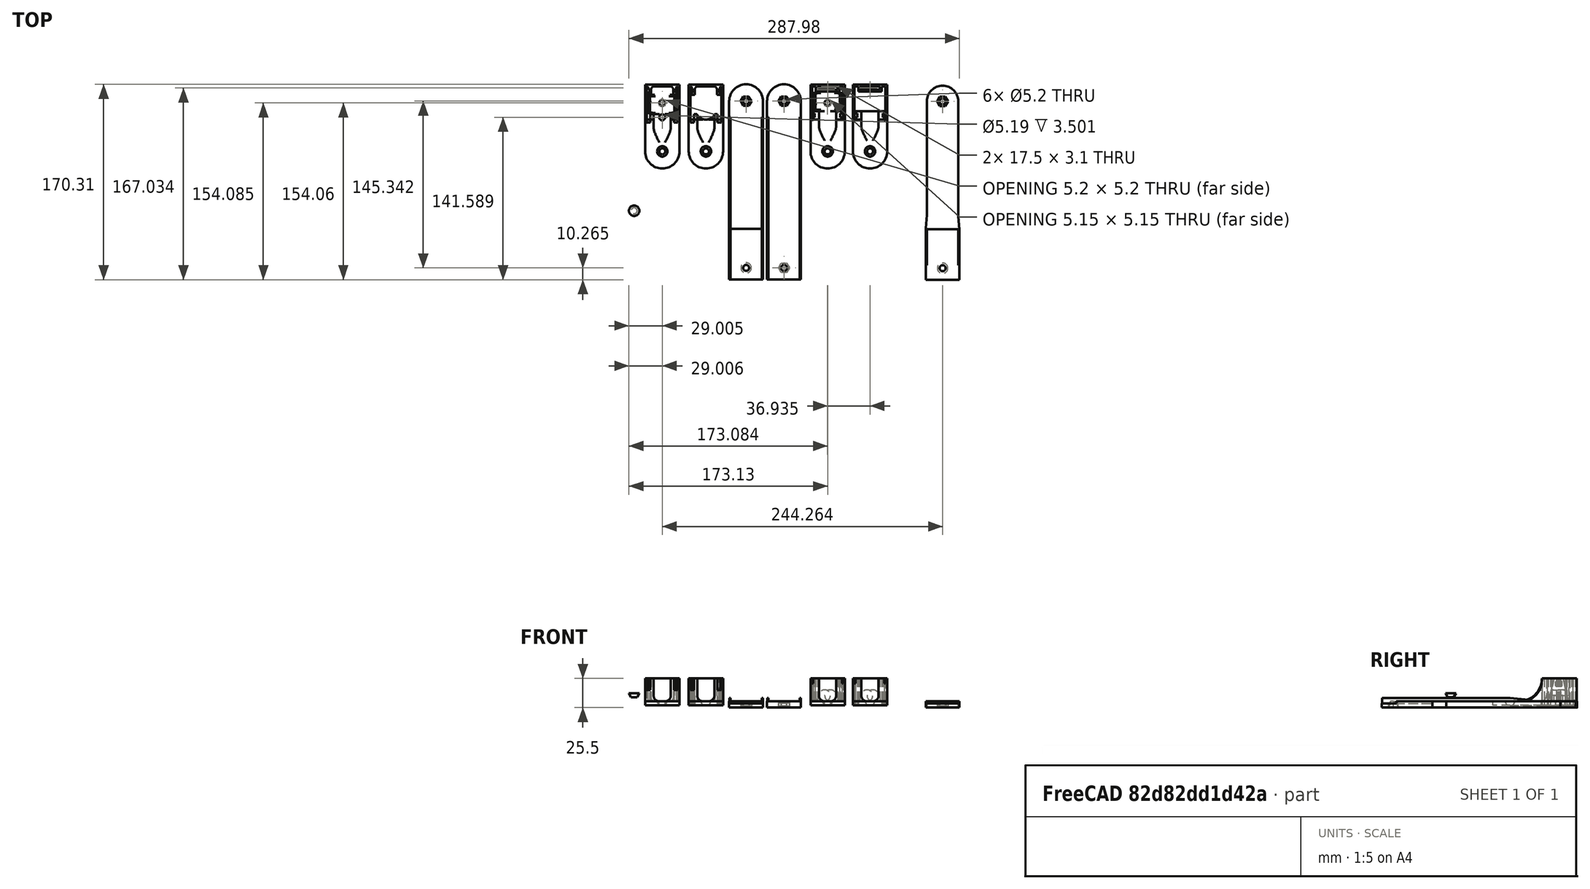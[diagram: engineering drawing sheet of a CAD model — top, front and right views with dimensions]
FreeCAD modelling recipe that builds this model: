
FCSTD DOCUMENT  (FreeCAD 0.20R29177 +426 (Git))
Label: lamp.hanger
License: All rights reserved
LicenseURL: http://en.wikipedia.org/wiki/All_rights_reserved
objects: Part::Cut×5, Part::Feature×5, Part::Extrusion×5, Part::MultiFuse×4, Part::Part2DObjectPython×4, Part::FeaturePython×2, App::DocumentObjectGroup×1, Part::Cone×1
note: 26 computed .brp shape members not serialized (recipe doc carries the construction recipe); baked Part::Feature solids carry a one-line shape summary decoded from their .brp

FEATURE [Part::MultiFuse] Fusion005002002014004003003002009002010004002003006003008008004007002004006006004008003005011012024  label="Reversed_Closed"
  Placement = pos=(139,-7e-15,-2.8e-14) rot=(0,0,1;0rad)
FEATURE [Part::Cut] Cut004006005004002008019023005008  label="Reversed_Open"
FEATURE [Part::MultiFuse] Fusion005002002014004003003002009002010004002003006003008008004007002004006006004008003005011013  label="Straight_Open"
FEATURE [Part::Feature] Fusion005002002014004003003002009002010004002003006003008008004007002004006006004008003005011006001  label="Console_Nut"
  shape: bbox 29.42 x 170 x 8.5 mm, 29 faces (baked)
FEATURE [Part::Feature] Fusion005002002014004003003002009002010004002003006003008008004007002004003001  label="Console_Screw"
  shape: bbox 29.42 x 170 x 8.5 mm, 24 faces (baked)
FEATURE [Part::Feature] Cut004006005004002008019023005046_solid  label="Straight_Closed"
  shape: bbox 29.86 x 73.08 x 23.5 mm, 156 faces (baked)
FEATURE [Part::Part2DObjectPython] Rectangle  # Draft 2D object (typed FeaturePython)
  ChamferSize = 0
  Columns = 1
  FilletRadius = 0
  Height = 7.4
  Length = 25
  MakeFace = true
  Placement = pos=(-687.019,-1.87622,16.3661) rot=(0,0,1;0rad)
  Rows = 1
FEATURE [Part::Extrusion] Extrusion
  Base = -> Rectangle
  Dir = (0,2.193e-13,-109.626)
  DirMode = 0
  FaceMakerClass = Part::FaceMakerBullseye
  LengthFwd = 0
  LengthRev = 0
  Solid = true
  Symmetric = false
FEATURE [Part::Cut] Cut
  Base = -> Fusion005002002014004003003002009002010004002003006003008008004007002004006006004008003005011013
  Tool = -> Extrusion
FEATURE [Part::Feature] Face
  Placement = pos=(54.9167,-4e-15,-2.5e-14) rot=(0,0,1;0rad)
  shape: bbox 29.86 x 8.799 x 4.951e-06 mm, 1 faces, 0 solids (baked)
FEATURE [Part::Extrusion] Extrusion001
  Base = -> Face
  Dir = (8.24e-14,-1.179e-13,15.3738)
  DirMode = 0
  FaceMakerClass = Part::FaceMakerBullseye
  LengthFwd = 0
  LengthRev = 0
  Placement = pos=(38.0168,1.181e-13,-15.3738) rot=(0,0,1;0rad)
  Solid = true
  Symmetric = false
FEATURE [Part::Feature] Face001
  Placement = pos=(92.9335,1.141e-13,-15.3738) rot=(0,0,1;0rad)
  shape: bbox 29.86 x 8.799 x 4.951e-06 mm, 1 faces, 0 solids (baked)
FEATURE [Part::Extrusion] Extrusion002
  Base = -> Face001
  Dir = (-4.36e-14,6.23e-14,-8.12616)
  DirMode = 0
  FaceMakerClass = Part::FaceMakerBullseye
  LengthFwd = 0
  LengthRev = 0
  Solid = true
  Symmetric = false
FEATURE [Part::MultiFuse] Fusion
  Shapes = -> [Extrusion002,Extrusion001]
FEATURE [Part::MultiFuse] Fusion005002002014004003003002009002010004002003006003008008004007002004006006004008003005011012025  label="Straight_Open001"
  Shapes = -> [Cut,Fusion]
FEATURE [Part::Part2DObjectPython] Rectangle001  # Draft 2D object (typed FeaturePython)
  ChamferSize = 0
  Columns = 1
  FilletRadius = 0
  Height = 42.3954
  Length = 36.2167
  MakeFace = true
  Placement = pos=(-548.432,-30.8896,16.3661) rot=(0,0,1;0rad)
  Rows = 1
  Support = -> [Cut004006005004002008019023005008]
FEATURE [Part::FeaturePython] Slice  # WARN: FeaturePython — macro-defined, semantics opaque (R4)
  Base = -> Cut004006005004002008019023005008
  Mode = 1
  Tolerance = 0
  Tools = -> [Rectangle001]
FEATURE [Part::FeaturePython] Slice_child0  label="Slice.0"  # WARN: FeaturePython — macro-defined, semantics opaque (R4)
  Base = -> Slice
  FilterType = 1
  Invert = false
  OverrideMaxVal = 0
  WindowFrom = 80
  WindowTo = 100
  items = 0
FEATURE [App::DocumentObjectGroup] GrExplode_Slice  label="Exploded Slice"
  Group = -> [Slice_child0]
FEATURE [Part::Cone] Cone
  Angle = 360
  AttacherType = Attacher::AttachEngine3D
  Height = 3.5
  Placement = pos=(-737,-103,0) rot=(0,0,1;0rad)
  Radius1 = 2.6
  Radius2 = 4.55
FEATURE [Part::Part2DObjectPython] Circle  # Draft 2D object (typed FeaturePython)
  FirstAngle = 0
  LastAngle = 0
  MakeFace = true
  Placement = pos=(-674.529,-14.4762,-3.63395) rot=(0,0,1;0rad)
  Radius = 9
FEATURE [Part::Extrusion] Extrusion003
  Base = -> Circle
  Dir = (0,0,190.437)
  DirMode = 0
  FaceMakerClass = Part::FaceMakerBullseye
  LengthFwd = 0
  LengthRev = 0
  Placement = pos=(0,0,-95.2184) rot=(0,0,1;0rad)
  Solid = true
  Symmetric = false
FEATURE [Part::Cut] Cut004006005004002008019023005009
  Base = -> Fusion005002002014004003003002009002010004002003006003008008004007002004006006004008003005011012025
  Tool = -> Extrusion003
FEATURE [Part::Cut] Cut007
  Placement = pos=(109.592,-0.265361,-6.8e-14) rot=(0,0,1;0rad)
FEATURE [Part::Part2DObjectPython] Rectangle002  # Draft 2D object (typed FeaturePython)
  Area = 489.027
  ChamferSize = 0
  Columns = 1
  FilletRadius = 0
  Height = 12.6
  Length = 38.8117
  MakeFace = true
  Placement = pos=(-487.643,-163.06,-5.63395) rot=(0,0,1;0rad)
  Rows = 1
FEATURE [Part::Extrusion] Extrusion004
  Base = -> Rectangle002
  Dir = (0,-5.4e-15,15.7521)
  DirMode = 0
  FaceMakerClass = Part::FaceMakerBullseye
  LengthFwd = 0
  LengthRev = 0
  Solid = true
  Symmetric = false
FEATURE [Part::Cut] Cut004006005004002008019023005010
  Base = -> Cut007
  Tool = -> Extrusion004
